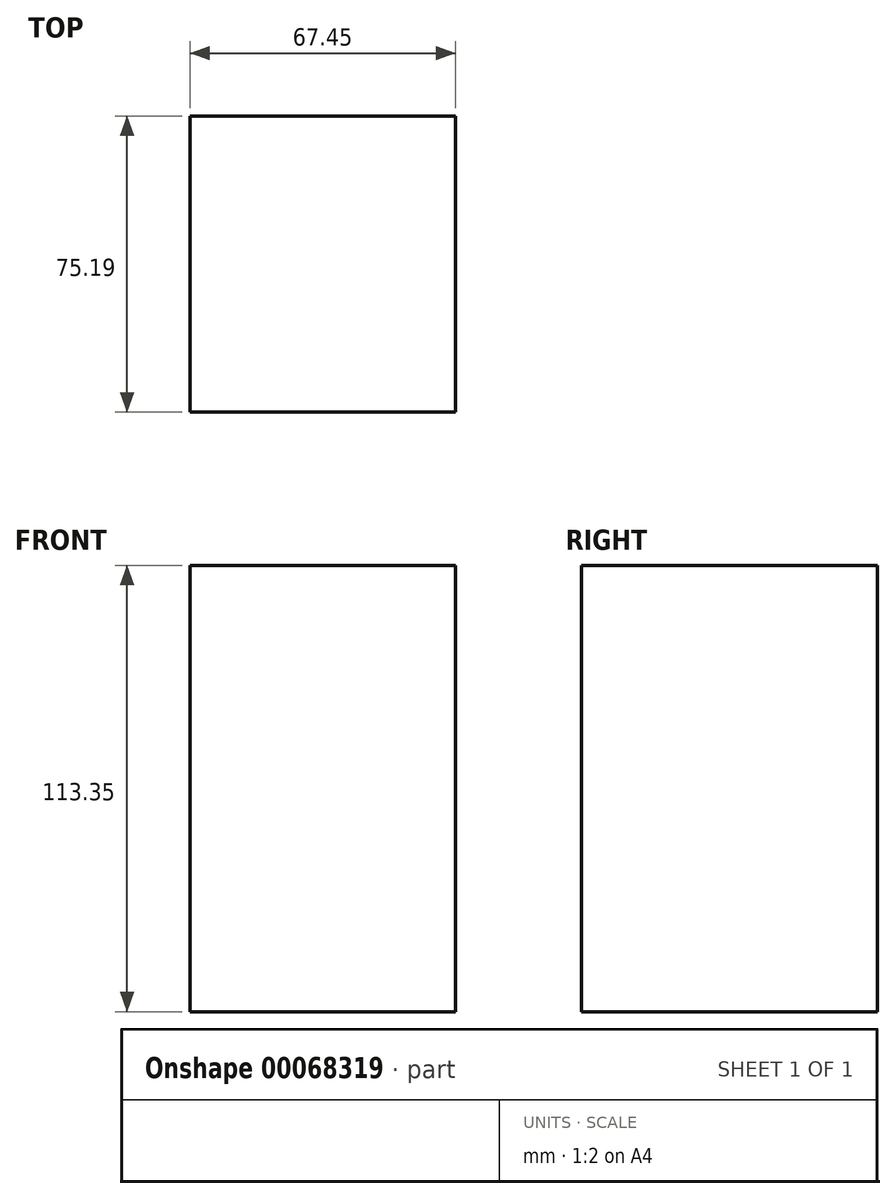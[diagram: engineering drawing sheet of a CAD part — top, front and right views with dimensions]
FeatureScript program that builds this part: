
annotation { "Feature Type Name" : "Feature", "Feature Type Description" : "" }
export const myFeature = defineFeature(function(context is Context, id is Id, definition is map)
    precondition{}
    {
        {
            var Q0;
            Q0=qCreatedBy(makeId("Top.planeOp"),FACE);
            var sketch = newSketch(context, id + "F0", { "sketchPlane" : qUnion([Q0])});
            skLineSegment(sketch, "E0.bottom", {"start": v(-35.1, -25.06) * mm, "end": v(32.35, -25.06) * mm});
            skLineSegment(sketch, "E0.top", {"start": v(-35.1, 50.13) * mm, "end": v(32.35, 50.13) * mm});
            skLineSegment(sketch, "E0.left", {"start": v(-35.1, -25.06) * mm, "end": v(-35.1, 50.13) * mm});
            skLineSegment(sketch, "E0.right", {"start": v(32.35, -25.06) * mm, "end": v(32.35, 50.13) * mm});
            skSolve(sketch);
        }
        {
            var Q0;
            Q0 = qSketchRegion(id + "F0", true);
            extrude(context, id + "F1", {"entities" : qUnion([Q0]), "depth" : 113.35 * mm});
        }
    });
